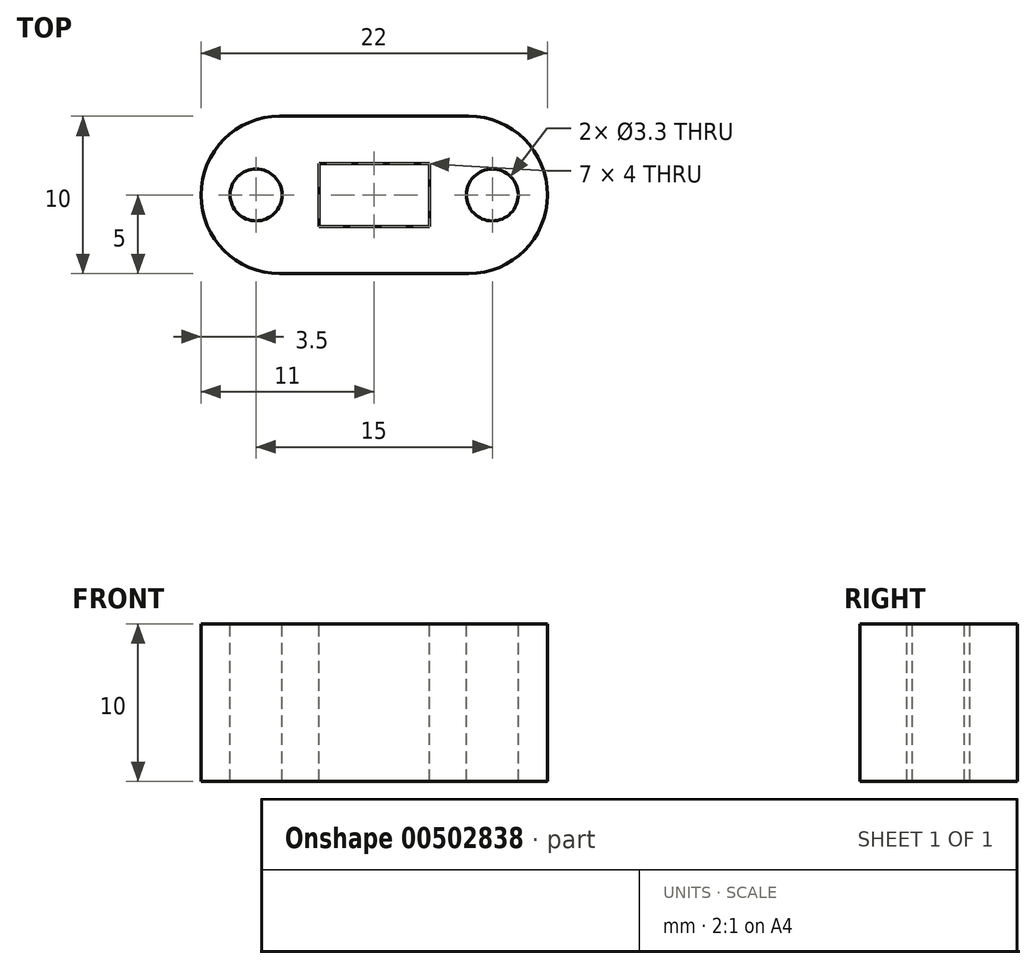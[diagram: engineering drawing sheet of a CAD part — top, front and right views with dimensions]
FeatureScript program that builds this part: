
annotation { "Feature Type Name" : "Feature", "Feature Type Description" : "" }
export const myFeature = defineFeature(function(context is Context, id is Id, definition is map)
    precondition{}
    {
        {
            var Q0;
            Q0=qCreatedBy(makeId("Top.planeOp"),FACE);
            var sketch = newSketch(context, id + "F0", { "sketchPlane" : qUnion([Q0])});
            skLineSegment(sketch, "E0.bottom", {"start": v(-11, 5) * mm, "end": v(11, 5) * mm});
            skLineSegment(sketch, "E0.top", {"start": v(-11, -5) * mm, "end": v(11, -5) * mm});
            skLineSegment(sketch, "E0.left", {"start": v(-11, 5) * mm, "end": v(-11, -5) * mm});
            skLineSegment(sketch, "E0.right", {"start": v(11, 5) * mm, "end": v(11, -5) * mm});
            skSolve(sketch);
        }
        {
            var Q0;
            Q0 = qSketchRegion(id + "F0", true);
            extrude(context, id + "F1", {"entities" : qUnion([Q0]), "depth" : 10 * mm});
        }
        {
            var Q0;
            Q0=makeQuery(id+"F1.opExtrude","CAP_FACE",FACE,{"disambiguationData":[OSD([sQuery(id+"F0.wireOp",EDGE,"E0.bottom"),sQuery(id+"F0.wireOp",EDGE,"E0.top"),sQuery(id+"F0.wireOp",EDGE,"E0.left"),sQuery(id+"F0.wireOp",EDGE,"E0.right")])],"isStart":false});
            var sketch = newSketch(context, id + "F2", { "sketchPlane" : qUnion([Q0])});
            skLineSegment(sketch, "E1", {"start": v(-7.5, 0) * mm, "end": v(7.5, 0) * mm, "construction": true});
            skCircle(sketch, "E2", {"center": v(-7.5, 0) * mm, "radius": 1.65 * mm});
            skCircle(sketch, "E3", {"center": v(7.5, 0) * mm, "radius": 1.65 * mm});
            skLineSegment(sketch, "E4.bottom", {"start": v(-3.5, 2) * mm, "end": v(3.5, 2) * mm});
            skLineSegment(sketch, "E4.top", {"start": v(-3.5, -2) * mm, "end": v(3.5, -2) * mm});
            skLineSegment(sketch, "E4.left", {"start": v(-3.5, 2) * mm, "end": v(-3.5, -2) * mm});
            skLineSegment(sketch, "E4.right", {"start": v(3.5, 2) * mm, "end": v(3.5, -2) * mm});
            skSolve(sketch);
        }
        {
            var Q0;
            Q0 = qSketchRegion(id + "F2", true);
            extrude(context, id + "F3", {"entities" : qUnion([Q0]), "operationType" : NewBodyOperationType.REMOVE, "endBound" : BoundingType.THROUGH_ALL, "oppositeDirection" : true, "depth" : 25 * mm});
        }
        {
            var Q0;
            Q0=makeQuery(id+"F1.opExtrude","SWEPT_EDGE",EDGE,{"disambiguationData":[OSD([sQuery(id+"F0.wireOp",EDGE,"E0.bottom"),sQuery(id+"F0.wireOp",EDGE,"E0.left")])]});
            var Q1;
            Q1=makeQuery(id+"F1.opExtrude","SWEPT_EDGE",EDGE,{"disambiguationData":[OSD([sQuery(id+"F0.wireOp",EDGE,"E0.top"),sQuery(id+"F0.wireOp",EDGE,"E0.left")])]});
            var Q2;
            Q2=makeQuery(id+"F1.opExtrude","SWEPT_EDGE",EDGE,{"disambiguationData":[OSD([sQuery(id+"F0.wireOp",EDGE,"E0.bottom"),sQuery(id+"F0.wireOp",EDGE,"E0.right")])]});
            var Q3;
            Q3=makeQuery(id+"F1.opExtrude","SWEPT_EDGE",EDGE,{"disambiguationData":[OSD([sQuery(id+"F0.wireOp",EDGE,"E0.top"),sQuery(id+"F0.wireOp",EDGE,"E0.right")])]});
            fillet(context, id + "F4", {"entities" : qUnion([Q0, Q1, Q2, Q3]), "radius" : 5 * mm, "tangentPropagation" : true, "allowEdgeOverflow" : false});
        }
    });
